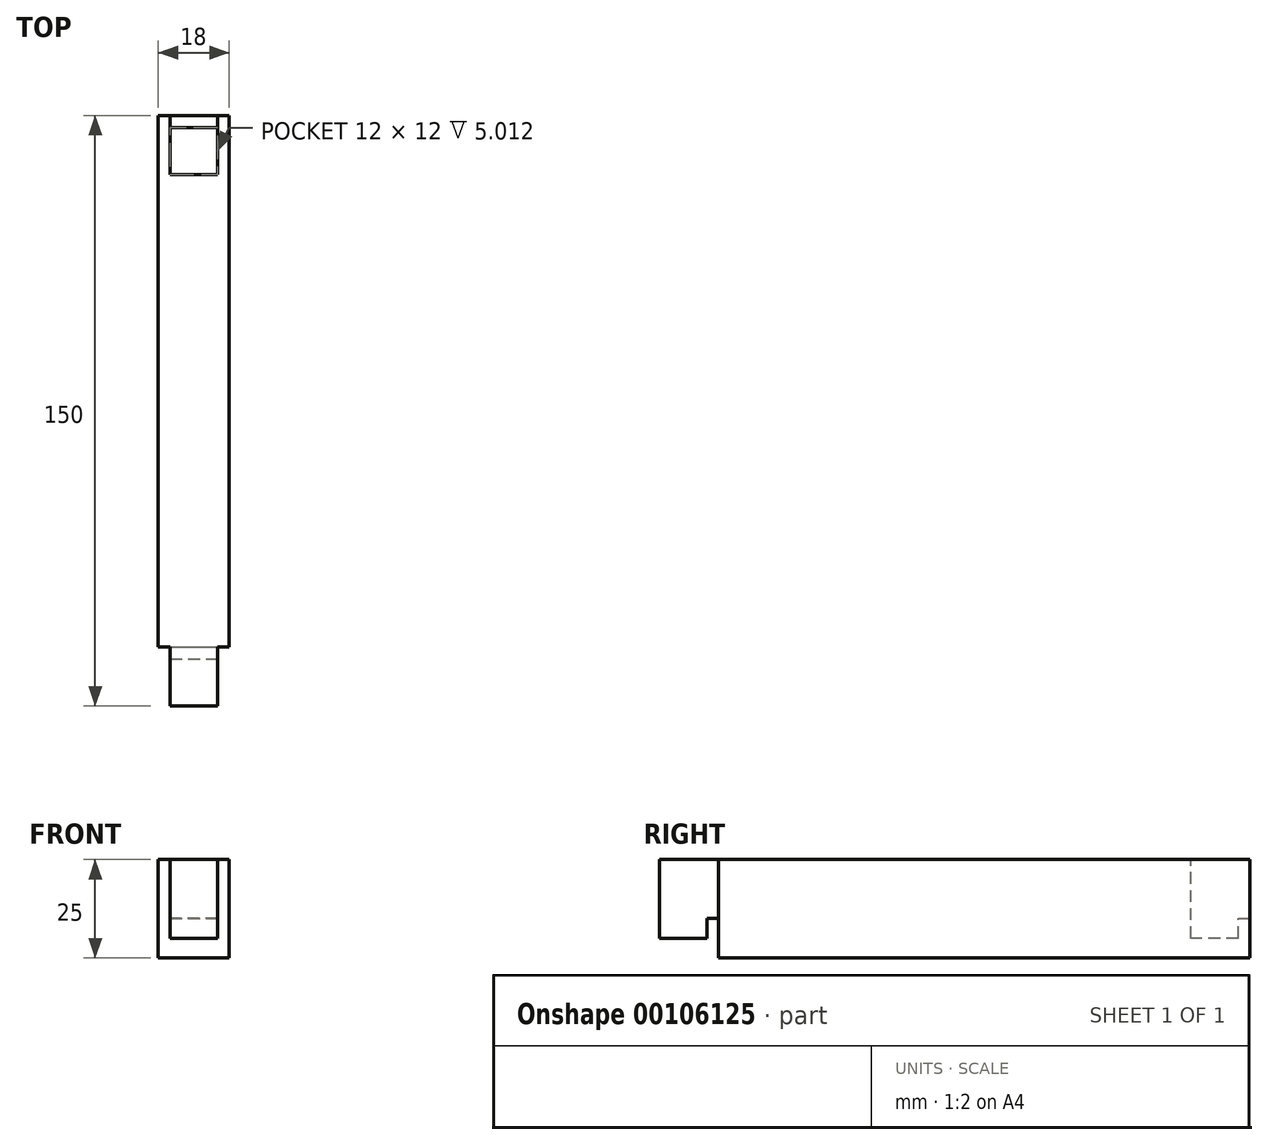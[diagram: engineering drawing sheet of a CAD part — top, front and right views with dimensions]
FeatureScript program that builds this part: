
annotation { "Feature Type Name" : "Feature", "Feature Type Description" : "" }
export const myFeature = defineFeature(function(context is Context, id is Id, definition is map)
    precondition{}
    {
        {
            var Q0;
            Q0=qCreatedBy(makeId("Front.planeOp"),FACE);
            var sketch = newSketch(context, id + "F0", { "sketchPlane" : qUnion([Q0])});
            skLineSegment(sketch, "E0.bottom", {"start": v(-9, 12.5) * mm, "end": v(9, 12.5) * mm});
            skLineSegment(sketch, "E0.top", {"start": v(-9, -12.5) * mm, "end": v(9, -12.5) * mm});
            skLineSegment(sketch, "E0.left", {"start": v(-9, 12.5) * mm, "end": v(-9, -12.5) * mm});
            skLineSegment(sketch, "E0.right", {"start": v(9, 12.5) * mm, "end": v(9, -12.5) * mm});
            skPoint(sketch, "E0.middle", {"position": v(0, 0) * mm});
            skSolve(sketch);
        }
        {
            var Q0;
            Q0=makeQuery(id+"F0.imprint","IMPRINT",FACE,{"disambiguationData":[TD([[makeQuery(id+"F0.imprint","IMPRINT",EDGE,{"derivedFrom":sQuery(id+"F0.wireOp",EDGE,"E0.bottom")}),-1.0]])]});
            extrude(context, id + "F1", {"entities" : qUnion([Q0]), "depth" : 150 * mm});
        }
        {
            var Q0;
            Q0=makeQuery(id+"F1.opExtrude","SWEPT_FACE",FACE,{"disambiguationData":[OSD([sQuery(id+"F0.wireOp",EDGE,"E0.right")])]});
            var sketch = newSketch(context, id + "F2", { "sketchPlane" : qUnion([Q0])});
            skLineSegment(sketch, "E1", {"start": v(-135, -12.5) * mm, "end": v(-135, -2.5) * mm});
            skLineSegment(sketch, "E2", {"start": v(-135, -2.5) * mm, "end": v(-138, -2.5) * mm});
            skLineSegment(sketch, "E3", {"start": v(-138, -2.5) * mm, "end": v(-138, -7.5) * mm});
            skLineSegment(sketch, "E4", {"start": v(-150, -7.5) * mm, "end": v(-138, -7.5) * mm});
            skSolve(sketch);
        }
        {
            var Q0;
            {var subQ5=sQuery(id+"F2.wireOp",EDGE,"E1");Q0=makeQuery(id+"F2.imprint","IMPRINT",FACE,{"disambiguationData":[TD([[makeQuery(id+"F2.imprint","IMPRINT",EDGE,{"derivedFrom":subQ5}),1.0]])]});}
            extrude(context, id + "F3", {"entities" : qUnion([Q0]), "operationType" : NewBodyOperationType.REMOVE, "oppositeDirection" : true, "depth" : 25 * mm});
        }
        {
            var Q0;
            Q0=makeQuery(id+"F1.opExtrude","SWEPT_FACE",FACE,{"disambiguationData":[OSD([sQuery(id+"F0.wireOp",EDGE,"E0.bottom")])]});
            var sketch = newSketch(context, id + "F4", { "sketchPlane" : qUnion([Q0])});
            skLineSegment(sketch, "E5.bottom", {"start": v(-6, 12.5) * mm, "end": v(6, 12.5) * mm});
            skLineSegment(sketch, "E5.top", {"start": v(-6, -7.5) * mm, "end": v(6, -7.5) * mm});
            skLineSegment(sketch, "E5.left", {"start": v(-6, 12.5) * mm, "end": v(-6, -7.5) * mm});
            skLineSegment(sketch, "E5.right", {"start": v(6, 12.5) * mm, "end": v(6, -7.5) * mm});
            skPoint(sketch, "E5.middle", {"position": v(0, 2.5) * mm});
            skLineSegment(sketch, "E6.bottom", {"start": v(9, -150) * mm, "end": v(6, -150) * mm});
            skLineSegment(sketch, "E6.top", {"start": v(9, -135) * mm, "end": v(6, -135) * mm});
            skLineSegment(sketch, "E6.left", {"start": v(9, -150) * mm, "end": v(9, -135) * mm});
            skLineSegment(sketch, "E6.right", {"start": v(6, -150) * mm, "end": v(6, -135) * mm});
            skLineSegment(sketch, "E7.bottom", {"start": v(-9, -150) * mm, "end": v(-6, -150) * mm});
            skLineSegment(sketch, "E7.top", {"start": v(-9, -135) * mm, "end": v(-6, -135) * mm});
            skLineSegment(sketch, "E7.left", {"start": v(-9, -150) * mm, "end": v(-9, -135) * mm});
            skLineSegment(sketch, "E7.right", {"start": v(-6, -150) * mm, "end": v(-6, -135) * mm});
            skSolve(sketch);
        }
        {
            var Q0;
            Q0=makeQuery(id+"F4.imprint","IMPRINT",FACE,{"disambiguationData":[TD([[makeQuery(id+"F4.imprint","IMPRINT",EDGE,{"derivedFrom":sQuery(id+"F4.wireOp",EDGE,"E6.bottom")}),1.0]])]});
            var Q1;
            Q1=makeQuery(id+"F4.imprint","IMPRINT",FACE,{"disambiguationData":[TD([[makeQuery(id+"F4.imprint","IMPRINT",EDGE,{"derivedFrom":sQuery(id+"F4.wireOp",EDGE,"E7.bottom")}),1.0]])]});
            extrude(context, id + "F5", {"entities" : qUnion([Q0, Q1]), "operationType" : NewBodyOperationType.REMOVE, "oppositeDirection" : true, "depth" : 25 * mm});
        }
        {
            var Q0;
            Q0=makeQuery(id+"F1.opExtrude","SWEPT_FACE",FACE,{"disambiguationData":[OSD([sQuery(id+"F0.wireOp",EDGE,"E0.bottom")])]});
            var sketch = newSketch(context, id + "F6", { "sketchPlane" : qUnion([Q0])});
            skLineSegment(sketch, "E8", {"start": v(0, 0) * mm, "end": v(0, -3) * mm, "construction": true});
            skLineSegment(sketch, "E9", {"start": v(9, -3) * mm, "end": v(-9, -3) * mm, "construction": true});
            skLineSegment(sketch, "E10.bottom", {"start": v(-6, -3) * mm, "end": v(6, -3) * mm});
            skLineSegment(sketch, "E10.top", {"start": v(-6, -15) * mm, "end": v(6, -15) * mm});
            skLineSegment(sketch, "E10.left", {"start": v(-6, -3) * mm, "end": v(-6, -15) * mm});
            skLineSegment(sketch, "E10.right", {"start": v(6, -3) * mm, "end": v(6, -15) * mm});
            skPoint(sketch, "E10.middle", {"position": v(0, -9) * mm});
            skSolve(sketch);
        }
        {
            var Q0;
            Q0=makeQuery(id+"F6.imprint","IMPRINT",FACE,{"disambiguationData":[TD([[makeQuery(id+"F6.imprint","IMPRINT",EDGE,{"derivedFrom":sQuery(id+"F6.wireOp",EDGE,"E10.bottom")}),-1.0]])]});
            extrude(context, id + "F7", {"entities" : qUnion([Q0]), "operationType" : NewBodyOperationType.REMOVE, "oppositeDirection" : true, "depth" : 20 * mm});
        }
        {
            var Q0;
            Q0=makeQuery(id+"F0.imprint","IMPRINT",FACE,{"disambiguationData":[TD([[makeQuery(id+"F0.imprint","IMPRINT",EDGE,{"derivedFrom":sQuery(id+"F0.wireOp",EDGE,"E0.bottom")}),-1.0]])]});
            var sketch = newSketch(context, id + "F8", { "sketchPlane" : qUnion([Q0])});
            skLineSegment(sketch, "E11.bottom", {"start": v(6, 12.51) * mm, "end": v(-6, 12.51) * mm});
            skLineSegment(sketch, "E11.top", {"start": v(6, -2.49) * mm, "end": v(-6, -2.49) * mm});
            skLineSegment(sketch, "E11.left", {"start": v(6, 12.51) * mm, "end": v(6, -2.49) * mm});
            skLineSegment(sketch, "E11.right", {"start": v(-6, 12.51) * mm, "end": v(-6, -2.49) * mm});
            skPoint(sketch, "E11.middle", {"position": v(0, 5.01) * mm});
            skSolve(sketch);
        }
        {
            var Q0;
            Q0 = qSketchRegion(id + "F8", true);
            extrude(context, id + "F9", {"entities" : qUnion([Q0]), "operationType" : NewBodyOperationType.REMOVE, "depth" : 5 * mm});
        }
    });
